# Revit family: FPB_FAN POWERED CONSTANT VOLUME_10-60
name_source: partatom
category: Mechanical Equipment
revit_build: Autodesk Revit 2016 (Build: 20161004_0715(x64)
units: mm (PartAtom-declared; Revit-internal decimal feet)

## family parameters
Always vertical = Yes
Cut with Voids When Loaded = No
Part Type = Normal
Room Calculation Point = No
Round Connector Dimension = Use Diameter
Shared = No
Work Plane-Based = No

## types (12) — shared parameters
Designation = FPB
Number of Poles = 3
PBA Load Classification = NC
Phase = 3
Side Clearance = 36"

## per-type parameters (varying)
- FDC5000 SIZE20(A=6): 90° Inlet Attenuator=FDC5000 90deg.INLET ATTENUATOR SIZES10-60 : 90 DEG. ATTENUATOR SIZE20; A=6"; B=14"; Boot Filter=FDC 5000 FILTER SIZE10-60 : FDC 5000 FILTER SIZE20; Bottom Electric box_Length=11 1/2"; Bottom Electric box_Width=14 5/32"; C=12 1/2"; D=12"; DIA=5 7/8"; Discharge Attenuator=FDC5000 DISCHARGE ATTENUATOR SIZES10-60 : FDC5000 DISCHARGE ATTENUATOR SIZE20; E=15 1/2"; Elec.Coil=ELECTRIC COIL FDC5000 : FDC5000 ELECTRIC COIL SIZE20; F=3"; H=17 1/2"; Hot water Coil=HOT WATER COIL WITH ACCESS DOOR FDC5000 : FDC5000 HOT WATER COIL SIZE20; INLET DISTANCE=4"; INLET LENGTH=9 1/2"; Inlet Attenuator=FDC5000 INLET ATTENUATOR SIZES10-60 : FDC5000 INLET ATTENUATOR SIZE20; L=25 1/2"; PBA Duct Outlet Height=12 1/2"; PBA Duct Outlet Width=14"; Power Factor=1; Voltage=480 V; W=31"; control box side adjustment=7 29/32"
- FDC5000 SIZE10(A=6): 90° Inlet Attenuator=FDC5000 90deg.INLET ATTENUATOR SIZES10-60 : 90 DEG. ATTENUATOR SIZE10; A=6"; B=12"; Boot Filter=FDC 5000 FILTER SIZE10-60 : FDC 5000 FILTER SIZE10; Bottom Electric box_Length=6"; Bottom Electric box_Width=16 21/32"; C=10"; D=8"; DIA=5 7/8"; Discharge Attenuator=FDC5000 DISCHARGE ATTENUATOR SIZES10-60 : FDC5000 DISCHARGE ATTENUATOR SIZE10; E=10"; Elec.Coil=ELECTRIC COIL FDC5000 : FDC5000 ELECTRIC COIL SIZE10; F=1 1/2"; H=12"; Hot water Coil=HOT WATER COIL WITH ACCESS DOOR FDC5000 : FDC5000 HOT WATER COIL SIZE10; INLET DISTANCE=4"; INLET LENGTH=4 3/8"; Inlet Attenuator=FDC5000 INLET ATTENUATOR SIZES10-60 : FDC5000 INLET ATTENUATOR SIZE10; L=28"; PBA Duct Outlet Height=10"; PBA Duct Outlet Width=12"; Power Factor=0; Voltage=0 V; W=18"; control box side adjustment=6 21/32"
- FDC5000 SIZE10(A=5): 90° Inlet Attenuator=FDC5000 90deg.INLET ATTENUATOR SIZES10-60 : 90 DEG. ATTENUATOR SIZE10; A=5"; B=12"; Boot Filter=FDC 5000 FILTER SIZE10-60 : FDC 5000 FILTER SIZE10; Bottom Electric box_Length=6"; Bottom Electric box_Width=16 21/32"; C=10"; D=8"; DIA=4 7/8"; Discharge Attenuator=FDC5000 DISCHARGE ATTENUATOR SIZES10-60 : FDC5000 DISCHARGE ATTENUATOR SIZE10; E=10"; Elec.Coil=ELECTRIC COIL FDC5000 : FDC5000 ELECTRIC COIL SIZE10; F=1 1/2"; H=12"; Hot water Coil=HOT WATER COIL WITH ACCESS DOOR FDC5000 : FDC5000 HOT WATER COIL SIZE10; INLET DISTANCE=3 1/2"; INLET LENGTH=4 3/8"; Inlet Attenuator=FDC5000 INLET ATTENUATOR SIZES10-60 : FDC5000 INLET ATTENUATOR SIZE10; L=28"; PBA Duct Outlet Height=10"; PBA Duct Outlet Width=12"; Power Factor=0; Voltage=0 V; W=18"; control box side adjustment=6 21/32"
- FDC5000 SIZE20(A=8): 90° Inlet Attenuator=FDC5000 90deg.INLET ATTENUATOR SIZES10-60 : 90 DEG. ATTENUATOR SIZE20; A=8"; B=14"; Boot Filter=FDC 5000 FILTER SIZE10-60 : FDC 5000 FILTER SIZE20; Bottom Electric box_Length=11 1/2"; Bottom Electric box_Width=14 5/32"; C=12 1/2"; D=12"; DIA=7 7/8"; Discharge Attenuator=FDC5000 DISCHARGE ATTENUATOR SIZES10-60 : FDC5000 DISCHARGE ATTENUATOR SIZE20; E=15 1/2"; Elec.Coil=ELECTRIC COIL FDC5000 : FDC5000 ELECTRIC COIL SIZE20; F=3"; H=17 1/2"; Hot water Coil=HOT WATER COIL WITH ACCESS DOOR FDC5000 : FDC5000 HOT WATER COIL SIZE20; INLET DISTANCE=5"; INLET LENGTH=9 1/2"; Inlet Attenuator=FDC5000 INLET ATTENUATOR SIZES10-60 : FDC5000 INLET ATTENUATOR SIZE20; L=25 1/2"; PBA Duct Outlet Height=12 1/2"; PBA Duct Outlet Width=14"; Power Factor=0; Voltage=0 V; W=31"; control box side adjustment=7 29/32"
- FDC5000 SIZE30(A=8): 90° Inlet Attenuator=FDC5000 90deg.INLET ATTENUATOR SIZES10-60 : 90 DEG. ATTENUATOR SIZE30; A=8"; B=14"; Boot Filter=FDC 5000 FILTER SIZE10-60 : FDC 5000 FILTER SIZE30; Bottom Electric box_Length=11 1/2"; Bottom Electric box_Width=14 5/32"; C=12 1/2"; D=12"; DIA=7 7/8"; Discharge Attenuator=FDC5000 DISCHARGE ATTENUATOR SIZES10-60 : FDC5000 DISCHARGE ATTENUATOR SIZE30; E=15 1/2"; Elec.Coil=ELECTRIC COIL FDC5000 : FDC5000 ELECTRIC COIL SIZE30; F=3"; H=17 1/2"; Hot water Coil=HOT WATER COIL WITH ACCESS DOOR FDC5000 : FDC5000 HOT WATER COIL SIZE30; INLET DISTANCE=5"; INLET LENGTH=9 1/2"; Inlet Attenuator=FDC5000 INLET ATTENUATOR SIZES10-60 : FDC5000 INLET ATTENUATOR SIZE30; L=25 1/2"; PBA Duct Outlet Height=12 1/2"; PBA Duct Outlet Width=14"; Power Factor=0; Voltage=0 V; W=31"; control box side adjustment=7 29/32"
- FDC5000 SIZE30(A=10): 90° Inlet Attenuator=FDC5000 90deg.INLET ATTENUATOR SIZES10-60 : 90 DEG. ATTENUATOR SIZE30; A=10"; B=14"; Boot Filter=FDC 5000 FILTER SIZE10-60 : FDC 5000 FILTER SIZE30; Bottom Electric box_Length=11 1/2"; Bottom Electric box_Width=14 5/32"; C=12 1/2"; D=12"; DIA=9 7/8"; Discharge Attenuator=FDC5000 DISCHARGE ATTENUATOR SIZES10-60 : FDC5000 DISCHARGE ATTENUATOR SIZE30; E=15 1/2"; Elec.Coil=ELECTRIC COIL FDC5000 : FDC5000 ELECTRIC COIL SIZE30; F=3"; H=17 1/2"; Hot water Coil=HOT WATER COIL WITH ACCESS DOOR FDC5000 : FDC5000 HOT WATER COIL SIZE30; INLET DISTANCE=6"; INLET LENGTH=9 1/2"; Inlet Attenuator=FDC5000 INLET ATTENUATOR SIZES10-60 : FDC5000 INLET ATTENUATOR SIZE30; L=25 1/2"; PBA Duct Outlet Height=12 1/2"; PBA Duct Outlet Width=14"; Power Factor=0; Voltage=480 V; W=31"; control box side adjustment=7 29/32"
- FDC5000 SIZE40(A=10): 90° Inlet Attenuator=FDC5000 90deg.INLET ATTENUATOR SIZES10-60 : 90 DEG. ATTENUATOR SIZE40; A=10"; B=16"; Boot Filter=FDC 5000 FILTER SIZE10-60 : FDC 5000 FILTER SIZE40; Bottom Electric box_Length=11 1/2"; Bottom Electric box_Width=18 5/32"; C=15"; D=16"; DIA=9 7/8"; Discharge Attenuator=FDC5000 DISCHARGE ATTENUATOR SIZES10-60 : FDC5000 DISCHARGE ATTENUATOR SIZE40; E=15 1/2"; Elec.Coil=ELECTRIC COIL FDC5000 : FDC5000 ELECTRIC COIL SIZE40; F=4"; H=17 1/2"; Hot water Coil=HOT WATER COIL WITH ACCESS DOOR FDC5000 : FDC5000 HOT WATER COIL SIZE40; INLET DISTANCE=6"; INLET LENGTH=9 1/2"; Inlet Attenuator=FDC5000 INLET ATTENUATOR SIZES10-60 : FDC5000 INLET ATTENUATOR SIZE40; L=29 1/2"; PBA Duct Outlet Height=15"; PBA Duct Outlet Width=16"; Power Factor=0; Voltage=0 V; W=35"; control box side adjustment=5 29/32"
- FDC5000 SIZE40(A=12): 90° Inlet Attenuator=FDC5000 90deg.INLET ATTENUATOR SIZES10-60 : 90 DEG. ATTENUATOR SIZE40; A=12"; B=16"; Boot Filter=FDC 5000 FILTER SIZE10-60 : FDC 5000 FILTER SIZE40; Bottom Electric box_Length=11 1/2"; Bottom Electric box_Width=18 5/32"; C=15"; D=16"; DIA=11 7/8"; Discharge Attenuator=FDC5000 DISCHARGE ATTENUATOR SIZES10-60 : FDC5000 DISCHARGE ATTENUATOR SIZE40; E=15 1/2"; Elec.Coil=ELECTRIC COIL FDC5000 : FDC5000 ELECTRIC COIL SIZE40; F=4"; H=17 1/2"; Hot water Coil=HOT WATER COIL WITH ACCESS DOOR FDC5000 : FDC5000 HOT WATER COIL SIZE40; INLET DISTANCE=7"; INLET LENGTH=9 1/2"; Inlet Attenuator=FDC5000 INLET ATTENUATOR SIZES10-60 : FDC5000 INLET ATTENUATOR SIZE40; L=29 1/2"; PBA Duct Outlet Height=15"; PBA Duct Outlet Width=16"; Power Factor=0; Voltage=0 V; W=35"; control box side adjustment=5 29/32"
- FDC5000 SIZE50(A=12): 90° Inlet Attenuator=FDC5000 90deg.INLET ATTENUATOR SIZES10-60 : 90 DEG. ATTENUATOR SIZE50; A=12"; B=20"; Boot Filter=FDC 5000 FILTER SIZE10-60 : FDC 5000 FILTER SIZE50; Bottom Electric box_Length=14"; Bottom Electric box_Width=26 21/32"; C=17 1/2"; D=21"; DIA=11 7/8"; Discharge Attenuator=FDC5000 DISCHARGE ATTENUATOR SIZES10-60 : FDC5000 DISCHARGE ATTENUATOR SIZE50; E=18"; Elec.Coil=ELECTRIC COIL FDC5000 : FDC5000 ELECTRIC COIL SIZE50; F=3"; H=20"; Hot water Coil=HOT WATER COIL WITH ACCESS DOOR FDC5000 : FDC5000 HOT WATER COIL SIZE50; INLET DISTANCE=7"; INLET LENGTH=4 3/8"; Inlet Attenuator=FDC5000 INLET ATTENUATOR SIZES10-60 : FDC5000 INLET ATTENUATOR SIZE50; L=38"; PBA Duct Outlet Height=17 1/2"; PBA Duct Outlet Width=20"; Power Factor=0; Voltage=0 V; W=40"; control box side adjustment=1 21/32"
- FDC5000 SIZE50(A=14): 90° Inlet Attenuator=FDC5000 90deg.INLET ATTENUATOR SIZES10-60 : 90 DEG. ATTENUATOR SIZE50; A=14"; B=20"; Boot Filter=FDC 5000 FILTER SIZE10-60 : FDC 5000 FILTER SIZE50; Bottom Electric box_Length=14"; Bottom Electric box_Width=26 21/32"; C=17 1/2"; D=21"; DIA=13 7/8"; Discharge Attenuator=FDC5000 DISCHARGE ATTENUATOR SIZES10-60 : FDC5000 DISCHARGE ATTENUATOR SIZE50; E=18"; Elec.Coil=ELECTRIC COIL FDC5000 : FDC5000 ELECTRIC COIL SIZE50; F=3"; H=20"; Hot water Coil=HOT WATER COIL WITH ACCESS DOOR FDC5000 : FDC5000 HOT WATER COIL SIZE50; INLET DISTANCE=8"; INLET LENGTH=4 3/8"; Inlet Attenuator=FDC5000 INLET ATTENUATOR SIZES10-60 : FDC5000 INLET ATTENUATOR SIZE50; L=38"; PBA Duct Outlet Height=17 1/2"; PBA Duct Outlet Width=20"; Power Factor=0; Voltage=0 V; W=40"; control box side adjustment=1 21/32"
- FDC5000 SIZE60(A=14): 90° Inlet Attenuator=FDC5000 90deg.INLET ATTENUATOR SIZES10-60 : 90 DEG. ATTENUATOR SIZE60; A=14"; B=24"; Boot Filter=FDC 5000 FILTER SIZE10-60 : FDC 5000 FILTER SIZE60; Bottom Electric box_Length=14"; Bottom Electric box_Width=26 21/32"; C=18"; D=21"; DIA=13 7/8"; Discharge Attenuator=FDC5000 DISCHARGE ATTENUATOR SIZES10-60 : FDC5000 DISCHARGE ATTENUATOR SIZE60; E=18"; Elec.Coil=ELECTRIC COIL FDC5000 : FDC5000 ELECTRIC COIL SIZE60; F=3"; H=20"; Hot water Coil=HOT WATER COIL WITH ACCESS DOOR FDC5000 : FDC5000 HOT WATER COIL SIZE60; INLET DISTANCE=8"; INLET LENGTH=4 3/8"; Inlet Attenuator=FDC5000 INLET ATTENUATOR SIZES10-60 : FDC5000 INLET ATTENUATOR SIZE60; L=38"; PBA Duct Outlet Height=18"; PBA Duct Outlet Width=24"; Power Factor=0; Voltage=0 V; W=46"; control box side adjustment=1 21/32"
- FDC5000 SIZE60(A=16): 90° Inlet Attenuator=FDC5000 90deg.INLET ATTENUATOR SIZES10-60 : 90 DEG. ATTENUATOR SIZE60; A=16"; B=24"; Boot Filter=FDC 5000 FILTER SIZE10-60 : FDC 5000 FILTER SIZE60; Bottom Electric box_Length=14"; Bottom Electric box_Width=26 21/32"; C=18"; D=21"; DIA=15 7/8"; Discharge Attenuator=FDC5000 DISCHARGE ATTENUATOR SIZES10-60 : FDC5000 DISCHARGE ATTENUATOR SIZE60; E=18"; Elec.Coil=ELECTRIC COIL FDC5000 : FDC5000 ELECTRIC COIL SIZE60; F=3"; H=20"; Hot water Coil=HOT WATER COIL WITH ACCESS DOOR FDC5000 : FDC5000 HOT WATER COIL SIZE60; INLET DISTANCE=9"; INLET LENGTH=4 3/8"; Inlet Attenuator=FDC5000 INLET ATTENUATOR SIZES10-60 : FDC5000 INLET ATTENUATOR SIZE60; L=38"; PBA Duct Outlet Height=18"; PBA Duct Outlet Width=24"; Power Factor=1; Voltage=480 V; W=46"; control box side adjustment=1 21/32"

## geometry (parser evidence)
native form markers: Blend x4, Sweep x22
no freeform markers — native parametric forms only
